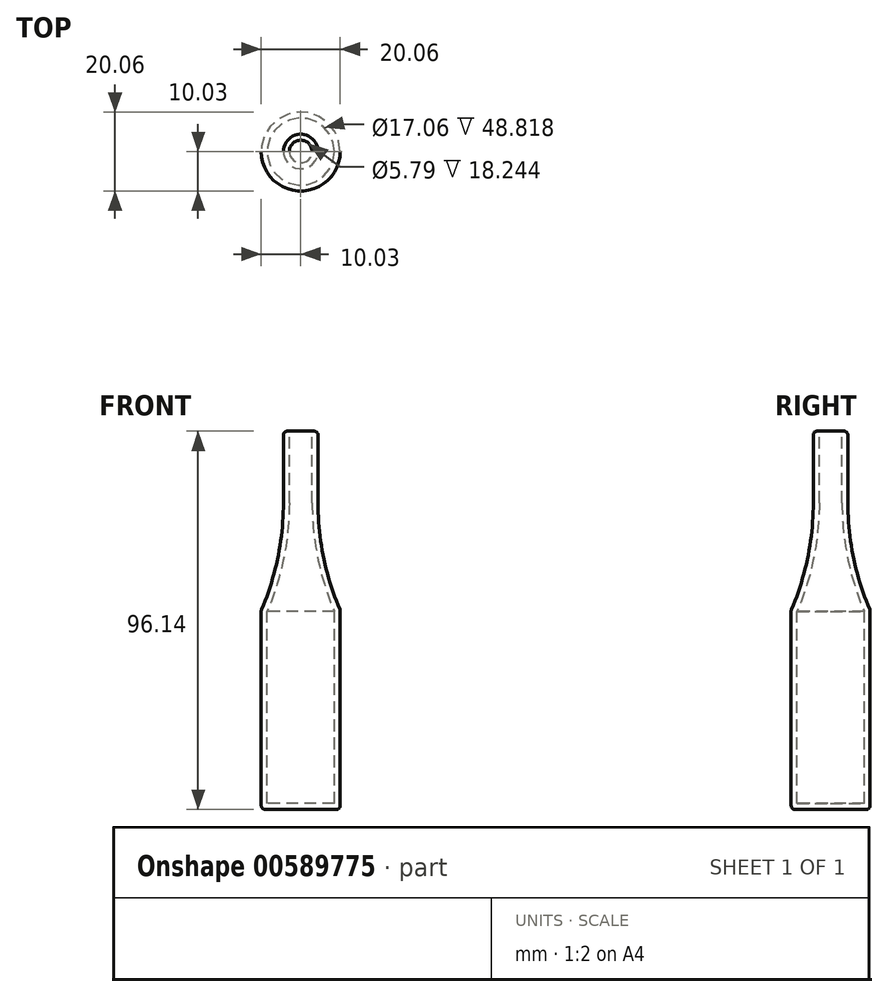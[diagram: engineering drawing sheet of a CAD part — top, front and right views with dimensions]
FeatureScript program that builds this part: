
annotation { "Feature Type Name" : "Feature", "Feature Type Description" : "" }
export const myFeature = defineFeature(function(context is Context, id is Id, definition is map)
    precondition{}
    {
        {
            var Q0;
            Q0=qCreatedBy(makeId("Front.planeOp"),FACE);
            var sketch = newSketch(context, id + "F0", { "sketchPlane" : qUnion([Q0])});
            skLineSegment(sketch, "E0", {"start": v(-10.03, 1.68) * mm, "end": v(-10.03, 52.3) * mm});
            skArc(sketch, "E1", {"start": v(-10.03, 52.3) * mm, "mid": v(-5.83, 65.65) * mm, "end": v(-4.4, 79.57) * mm});
            skLineSegment(sketch, "E2", {"start": v(-4.4, 79.57) * mm, "end": v(-4.4, 97.82) * mm});
            skLineSegment(sketch, "E3", {"start": v(-4.4, 97.82) * mm, "end": v(0, 97.82) * mm});
            skLineSegment(sketch, "E4", {"start": v(0, 97.82) * mm, "end": v(0, 1.68) * mm});
            skLineSegment(sketch, "E5", {"start": v(0, 1.68) * mm, "end": v(-10.03, 1.68) * mm});
            skSolve(sketch);
        }
        {
            var Q0;
            Q0 = qSketchRegion(id + "F0", true);
            var Q1;
            Q1=sQuery(id+"F0.wireOp",EDGE,"E4");
            revolve(context, id + "F1", {"entities" : qUnion([Q0]), "axis" : qUnion([Q1]), "revolveType" : RevolveType.FULL});
        }
        {
            var Q0;
            Q0=makeQuery(id+"F1.opRevolve","SWEPT_EDGE",EDGE,{"disambiguationData":[OSD([sQuery(id+"F0.wireOp",EDGE,"E0"),sQuery(id+"F0.wireOp",EDGE,"E1")])]});
            var Q1;
            Q1=makeQuery(id+"F1.opRevolve","SWEPT_EDGE",EDGE,{"disambiguationData":[OSD([sQuery(id+"F0.wireOp",EDGE,"E1"),sQuery(id+"F0.wireOp",EDGE,"E2")])]});
            var Q2;
            Q2=makeQuery(id+"F1.opRevolve","SWEPT_EDGE",EDGE,{"disambiguationData":[OSD([sQuery(id+"F0.wireOp",EDGE,"E2"),sQuery(id+"F0.wireOp",EDGE,"E3")])]});
            var Q3;
            Q3=makeQuery(id+"F1.opRevolve","SWEPT_EDGE",EDGE,{"disambiguationData":[OSD([sQuery(id+"F0.wireOp",EDGE,"E0"),sQuery(id+"F0.wireOp",EDGE,"E5")])]});
            fillet(context, id + "F2", {"entities" : qUnion([Q0, Q1, Q2, Q3]), "radius" : 1 * mm, "tangentPropagation" : true, "allowEdgeOverflow" : false});
        }
        {
            var Q0;
            Q0=makeQuery(id+"F1.opRevolve","SWEPT_FACE",FACE,{"disambiguationData":[OSD([sQuery(id+"F0.wireOp",EDGE,"E3")])]});
            shell(context, id + "F3", {"entities" : qUnion([Q0]), "thickness" : 1.5 * mm});
        }
    });
